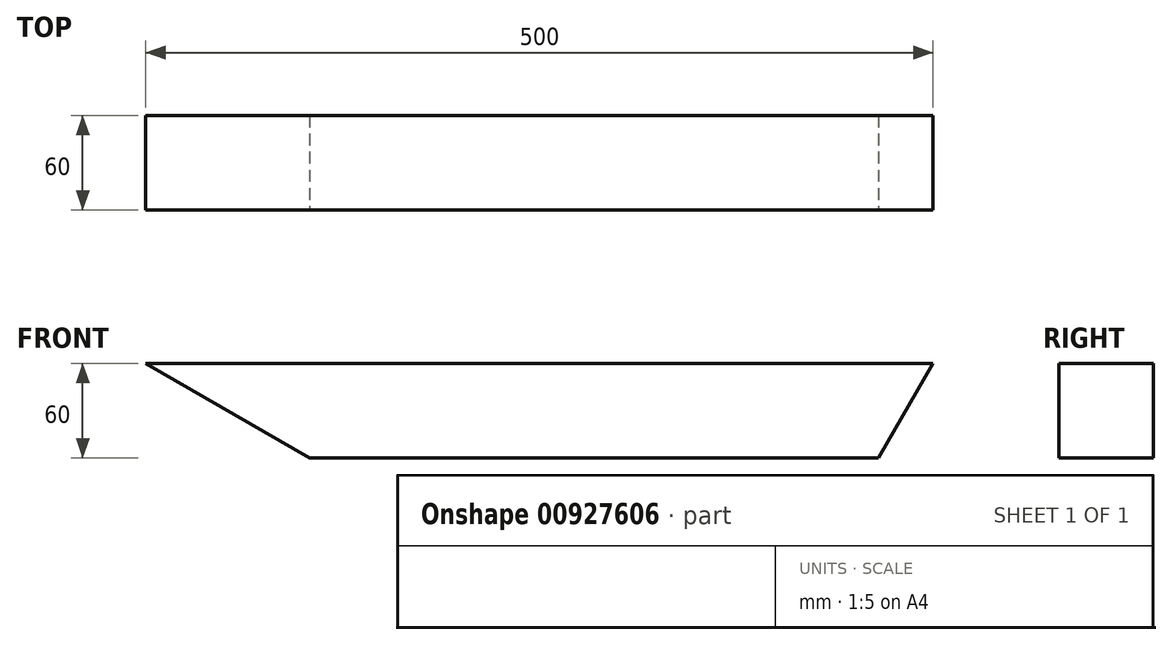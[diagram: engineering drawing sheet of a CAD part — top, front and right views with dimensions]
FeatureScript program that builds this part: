
annotation { "Feature Type Name" : "Feature", "Feature Type Description" : "" }
export const myFeature = defineFeature(function(context is Context, id is Id, definition is map)
    precondition{}
    {
        {
            var Q0;
            Q0=qCreatedBy(makeId("Right.planeOp"),FACE);
            var sketch = newSketch(context, id + "F0", { "sketchPlane" : qUnion([Q0])});
            skLineSegment(sketch, "E0.bottom", {"start": v(0, 0) * mm, "end": v(60, 0) * mm});
            skLineSegment(sketch, "E0.top", {"start": v(0, 60) * mm, "end": v(60, 60) * mm});
            skLineSegment(sketch, "E0.left", {"start": v(0, 0) * mm, "end": v(0, 60) * mm});
            skLineSegment(sketch, "E0.right", {"start": v(60, 0) * mm, "end": v(60, 60) * mm});
            skSolve(sketch);
        }
        {
            var Q0;
            Q0=makeQuery(id+"F0.imprint","IMPRINT",FACE,{"disambiguationData":[TD([[makeQuery(id+"F0.imprint","IMPRINT",EDGE,{"derivedFrom":sQuery(id+"F0.wireOp",EDGE,"E0.bottom")}),1.0]])]});
            extrude(context, id + "F1", {"entities" : qUnion([Q0]), "oppositeDirection" : true, "depth" : 500 * mm, "offsetDistance" : 25 * mm});
        }
        {
            var Q0;
            Q0=makeQuery(id+"F1.opExtrude","SWEPT_FACE",FACE,{"disambiguationData":[OSD([sQuery(id+"F0.wireOp",EDGE,"E0.left")])]});
            var sketch = newSketch(context, id + "F2", { "sketchPlane" : qUnion([Q0])});
            skLineSegment(sketch, "E1", {"start": v(0, 60) * mm, "end": v(-34.64, 0) * mm});
            skLineSegment(sketch, "E2", {"start": v(-500, 60) * mm, "end": v(-396.08, 0) * mm});
            skSolve(sketch);
        }
        {
            var Q0;
            {var subQ0=sQuery(id+"F2.wireOp",EDGE,"E2");Q0=makeQuery(id+"F2.imprint","IMPRINT",FACE,{"disambiguationData":[TD([[makeQuery(id+"F2.imprint","IMPRINT",EDGE,{"derivedFrom":subQ0}),-1.0]])]});}
            var Q1;
            {var subQ0=sQuery(id+"F2.wireOp",EDGE,"E1");Q1=makeQuery(id+"F2.imprint","IMPRINT",FACE,{"disambiguationData":[TD([[makeQuery(id+"F2.imprint","IMPRINT",EDGE,{"derivedFrom":subQ0}),1.0]])]});}
            extrude(context, id + "F3", {"entities" : qUnion([Q0, Q1]), "operationType" : NewBodyOperationType.REMOVE, "endBound" : BoundingType.THROUGH_ALL, "oppositeDirection" : true, "depth" : 25 * mm, "offsetDistance" : 25 * mm});
        }
    });
